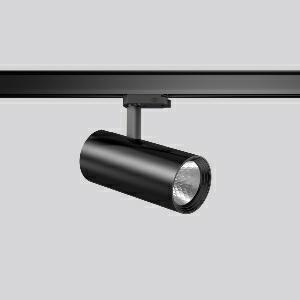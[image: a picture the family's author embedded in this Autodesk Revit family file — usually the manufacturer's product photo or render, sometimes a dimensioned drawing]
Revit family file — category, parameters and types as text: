
# Revit family: deecos_s_mini_742196_003_1_76_e1b4
name_source: partatom
category: Lighting Fixtures
units: mm (PartAtom-declared; Revit-internal decimal feet)

## family parameters
Cut with Voids When Loaded = No
Host = Face
Light Source = No
Part Type = Normal
Room Calculation Point = No
Round Connector Dimension = Use Diameter
Shared = No

## types (1)
- DEECOS S mini (1 x LED Modul 940, 2600 lm, 4000)
    Apparent Load = 20 VA
    Approval mark = CE
    CIE Flux Codes = 99 100 100 100 100
    Color Rendering = 92
    Color Temperature = 4000
    Default Elevation = 1800 mm
    Description = Series: DEECOS S mini
LED surface-mounted projector in modern design with no visible cooling ribs. Housing: die-cast aluminium, powder-coated. Rotation range: 356°. Swivel range: 90°. Black plastic ring and recessed LED to prevent glare from the side. Optical assembly with reflector made of MIRO-Silver with 98% total light reflection for outstanding efficiency - can be changed without tools. Best colour rendering index Ra>90. With adapter for RZB 3-circuit DALI tracks. Suitable for Track on ceiling, Wall track. High quality converter without flickering and stroboscopic effect. The following accessories can be mounted without use of tools: interchangeable lenses, decorative glasses, honeycomb louvre, clear and frosted diffusers, white interchangeable plastic ring. 
Colour: deep black, matt (RAL 9005)
Diameter: 87 mm
Height: 214 mm
Lamp: LED
Socket: without socket
Colour temperature: 4000K
Colour rendering index (CRI): 92
System power: 20 W
Rated luminous flux: 2600 lm
Luminous efficiency: 130 lm/W
Control gear: Converter, dimmable, DALI
Protection class: I
Type of protection: IP 20
    Height = 214 mm
    Lamp = 1 x LED Modul 940
    Lamp Light Flux = 2600 lm
    Lamp count = 1
    Length = 87 mm
    Lifetime = 50000 h
    Luminous efficacy = 130 lm/W
    Manufacturer = RZB
    ModVariant = No
    Model = 742196.003.1.76
    Mounting Place = Ceiling
    Mounting Type = Rail mounted
    Number of Poles = 1
    OnlyDefault = Yes
    Power Factor = 1
    Product Name = DEECOS S mini
    Product group = Track mounted projectors
    ProductGroupID = 301
    Protection Class = Protection class I
    Protection Degree = IP 20
    RLX_Detail_Level = 1
    RLX_Emergency_Light_Flux = 0 lm
    RLX_Emergency_Type = 0
    RLX_Emergency_Type_DB = No
    RlxData = <blob elided: 38545 chars, md5=d3d7958d>
    Socket = socket
    Standby Power = 0 W
    System Light Flux = 2600 lm
    System Power = 20 W
    Type Comments = Product without accessories
    Type Image = 741926.003.jpg
    URL = http://relux.com
    VarID = ---
    Voltage = 230 V
    Voltage Range = 220-240 V
    Weight = 0.00 kg
    Width = 0 mm  [stored 0 ft]

note: [stored X ft] marks values corroborated as IEEE doubles in the binary element streams (Revit-internal decimal feet)

## geometry (parser evidence)
native form markers: Blend x4, Sweep x11
no freeform markers — native parametric forms only
